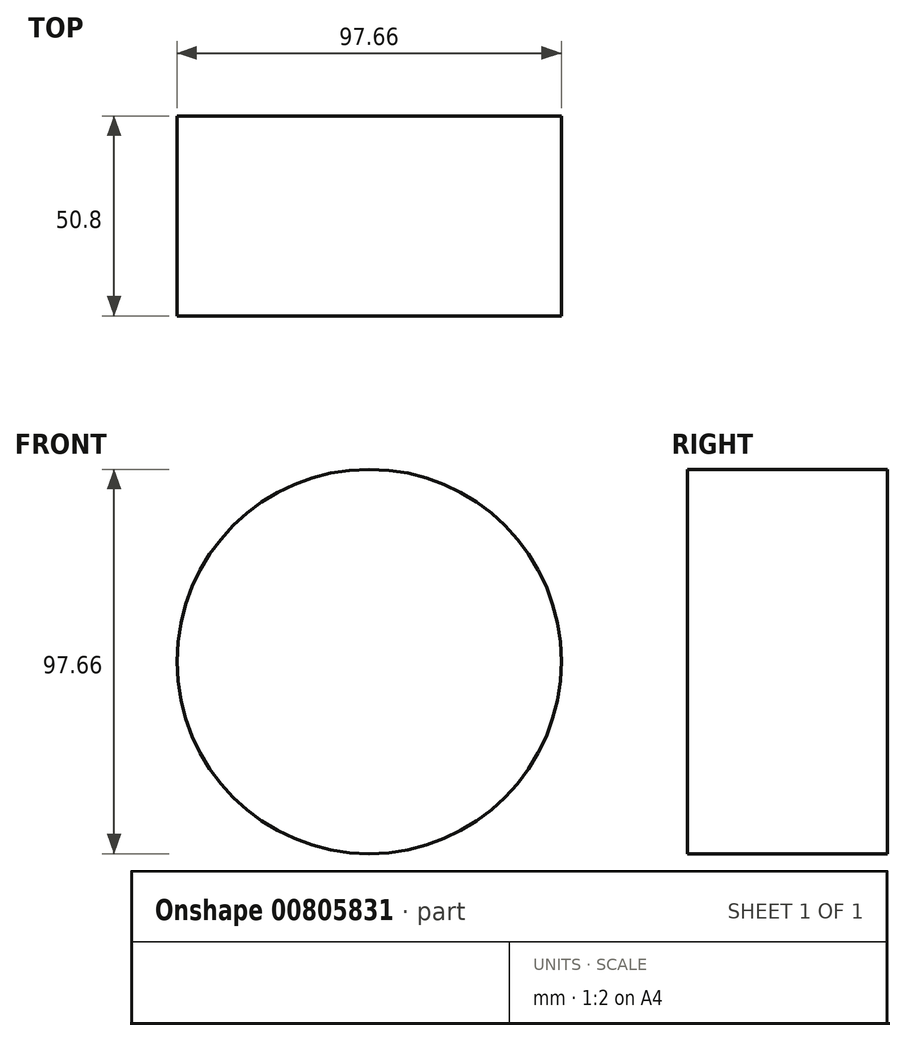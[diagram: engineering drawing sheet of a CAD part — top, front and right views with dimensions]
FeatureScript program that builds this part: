
annotation { "Feature Type Name" : "Feature", "Feature Type Description" : "" }
export const myFeature = defineFeature(function(context is Context, id is Id, definition is map)
    precondition{}
    {
        {
            var Q0;
            Q0=qCreatedBy(makeId("Front.planeOp"),FACE);
            var sketch = newSketch(context, id + "F0", { "sketchPlane" : qUnion([Q0])});
            skCircle(sketch, "E0", {"center": v(0, 0) * mm, "radius": 48.83 * mm});
            skSolve(sketch);
        }
        {
            var Q0;
            Q0 = qSketchRegion(id + "F0", true);
            extrude(context, id + "F1", {"entities" : qUnion([Q0]), "depth" : 50.8 * mm, "offsetDistance" : 25.4 * mm});
        }
    });
